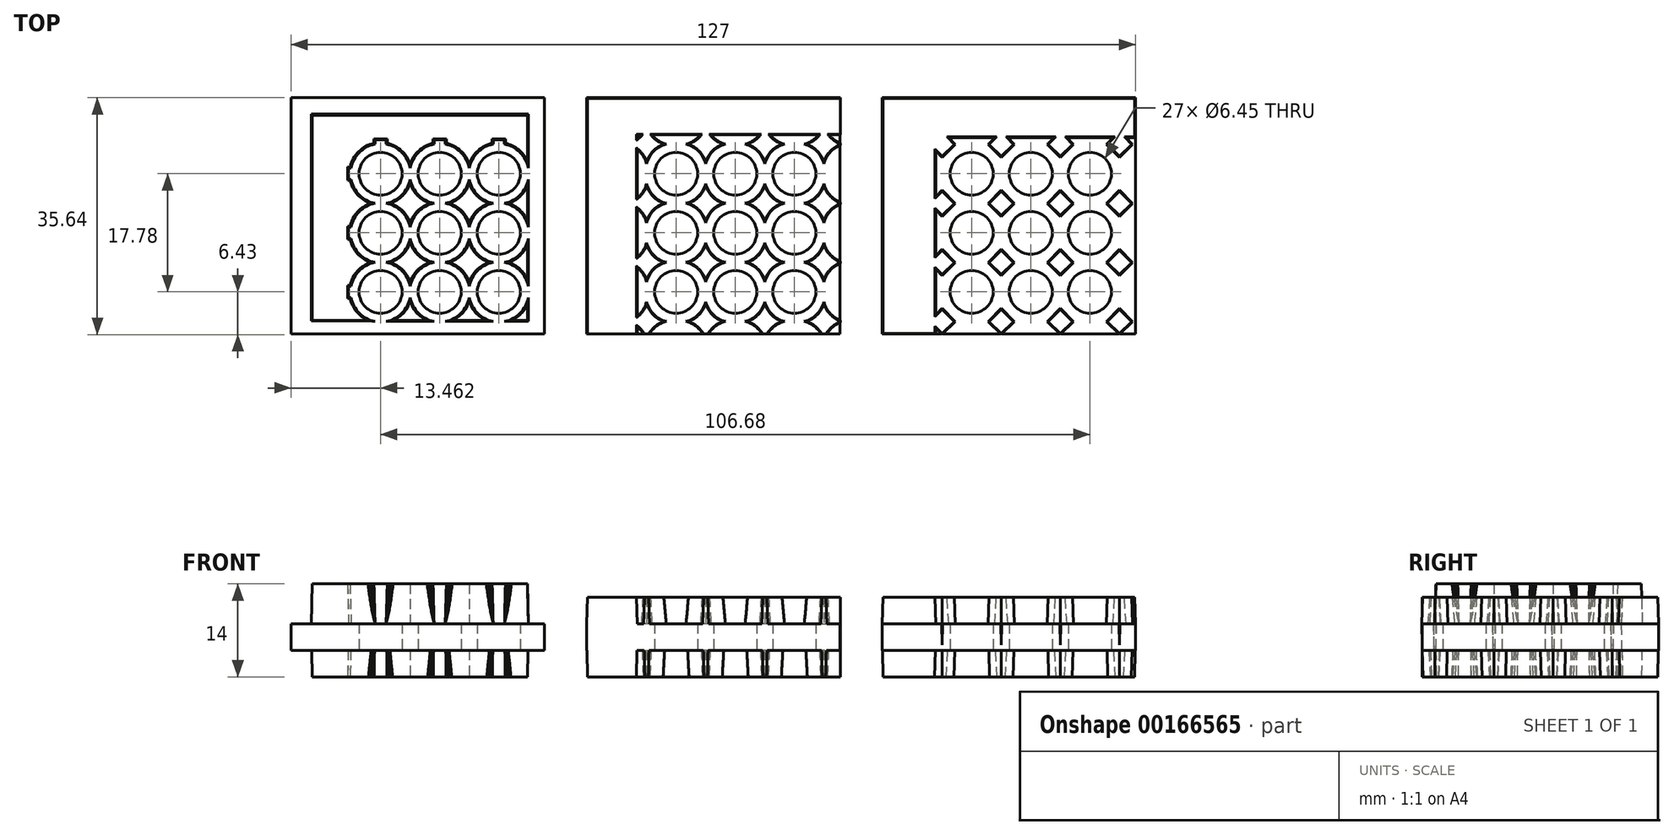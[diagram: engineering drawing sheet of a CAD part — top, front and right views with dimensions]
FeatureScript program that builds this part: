
annotation { "Feature Type Name" : "Feature", "Feature Type Description" : "" }
export const myFeature = defineFeature(function(context is Context, id is Id, definition is map)
    precondition{}
    {
        {
            var Q0;
            Q0=qCreatedBy(makeId("Top.planeOp"),FACE);
            var sketch = newSketch(context, id + "F0", { "sketchPlane" : qUnion([Q0])});
            skLineSegment(sketch, "E0.bottom", {"start": v(0, 0) * mm, "end": v(-38.1, 0) * mm});
            skLineSegment(sketch, "E0.top", {"start": v(0, 35.56) * mm, "end": v(-38.1, 35.56) * mm});
            skLineSegment(sketch, "E0.left", {"start": v(0, 0) * mm, "end": v(0, 35.56) * mm});
            skLineSegment(sketch, "E0.right", {"start": v(-38.1, 0) * mm, "end": v(-38.1, 35.56) * mm});
            skLineSegment(sketch, "E1.bottom", {"start": v(-44.45, 0) * mm, "end": v(-82.55, 0) * mm});
            skLineSegment(sketch, "E1.top", {"start": v(-44.45, 35.56) * mm, "end": v(-82.55, 35.56) * mm});
            skLineSegment(sketch, "E1.left", {"start": v(-44.45, 0) * mm, "end": v(-44.45, 35.56) * mm});
            skLineSegment(sketch, "E1.right", {"start": v(-82.55, 0) * mm, "end": v(-82.55, 35.56) * mm});
            skLineSegment(sketch, "E2.bottom", {"start": v(-88.9, 0) * mm, "end": v(-127, 0) * mm});
            skLineSegment(sketch, "E2.top", {"start": v(-88.9, 35.56) * mm, "end": v(-127, 35.56) * mm});
            skLineSegment(sketch, "E2.left", {"start": v(-88.9, 0) * mm, "end": v(-88.9, 35.56) * mm});
            skLineSegment(sketch, "E2.right", {"start": v(-127, 0) * mm, "end": v(-127, 35.56) * mm});
            skLineSegment(sketch, "E3.bottom", {"start": v(-44.45, 0) * mm, "end": v(-38.1, 0) * mm, "construction": true});
            skLineSegment(sketch, "E3.top", {"start": v(-44.45, 0) * mm, "end": v(-38.1, 0) * mm, "construction": true});
            skLineSegment(sketch, "E3.left", {"start": v(-44.45, 0) * mm, "end": v(-44.45, 0) * mm});
            skLineSegment(sketch, "E3.right", {"start": v(-38.1, 0) * mm, "end": v(-38.1, 0) * mm});
            skLineSegment(sketch, "E4.bottom", {"start": v(-88.9, 0) * mm, "end": v(-82.55, 0) * mm, "construction": true});
            skLineSegment(sketch, "E4.top", {"start": v(-88.9, 0) * mm, "end": v(-82.55, 0) * mm, "construction": true});
            skLineSegment(sketch, "E4.left", {"start": v(-88.9, 0) * mm, "end": v(-88.9, 0) * mm});
            skLineSegment(sketch, "E4.right", {"start": v(-82.55, 0) * mm, "end": v(-82.55, 0) * mm});
            skLineSegment(sketch, "E5.bottom", {"start": v(-88.9, 0) * mm, "end": v(-118.41, 0) * mm, "construction": true});
            skLineSegment(sketch, "E5.top", {"start": v(-88.9, 29.8) * mm, "end": v(-118.41, 29.8) * mm, "construction": true});
            skLineSegment(sketch, "E5.left", {"start": v(-88.9, 0) * mm, "end": v(-88.9, 29.8) * mm, "construction": true});
            skLineSegment(sketch, "E5.right", {"start": v(-118.41, 0) * mm, "end": v(-118.41, 29.8) * mm, "construction": true});
            skLineSegment(sketch, "E6.bottom", {"start": v(-44.45, 0) * mm, "end": v(-73.96, 0) * mm, "construction": true});
            skLineSegment(sketch, "E6.top", {"start": v(-44.45, 29.8) * mm, "end": v(-73.96, 29.8) * mm, "construction": true});
            skLineSegment(sketch, "E6.left", {"start": v(-44.45, 0) * mm, "end": v(-44.45, 29.8) * mm, "construction": true});
            skLineSegment(sketch, "E6.right", {"start": v(-73.96, 0) * mm, "end": v(-73.96, 29.8) * mm, "construction": true});
            skLineSegment(sketch, "E7.bottom", {"start": v(0, 0) * mm, "end": v(-29.51, 0) * mm, "construction": true});
            skLineSegment(sketch, "E7.top", {"start": v(0, 29.8) * mm, "end": v(-29.51, 29.8) * mm, "construction": true});
            skLineSegment(sketch, "E7.left", {"start": v(0, 0) * mm, "end": v(0, 29.8) * mm, "construction": true});
            skLineSegment(sketch, "E7.right", {"start": v(-29.51, 0) * mm, "end": v(-29.51, 29.8) * mm, "construction": true});
            skCircle(sketch, "E8", {"center": v(-113.54, 24.13) * mm, "radius": 3.23 * mm});
            skCircle(sketch, "E9", {"center": v(-69.09, 24.13) * mm, "radius": 3.23 * mm});
            skCircle(sketch, "E10", {"center": v(-24.64, 24.13) * mm, "radius": 3.23 * mm});
            skCircle(sketch, "E11.0.1.0", {"center": v(-113.54, 15.24) * mm, "radius": 3.23 * mm});
            skCircle(sketch, "E11.0.1.1", {"center": v(-69.09, 15.24) * mm, "radius": 3.23 * mm});
            skCircle(sketch, "E11.0.1.2", {"center": v(-24.64, 15.24) * mm, "radius": 3.23 * mm});
            skCircle(sketch, "E11.0.2.0", {"center": v(-113.54, 6.35) * mm, "radius": 3.23 * mm});
            skCircle(sketch, "E11.0.2.1", {"center": v(-69.09, 6.35) * mm, "radius": 3.23 * mm});
            skCircle(sketch, "E11.0.2.2", {"center": v(-24.64, 6.35) * mm, "radius": 3.23 * mm});
            skCircle(sketch, "E11.1.0.0", {"center": v(-104.65, 24.13) * mm, "radius": 3.23 * mm});
            skCircle(sketch, "E11.1.0.1", {"center": v(-60.2, 24.13) * mm, "radius": 3.23 * mm});
            skCircle(sketch, "E11.1.0.2", {"center": v(-15.75, 24.13) * mm, "radius": 3.23 * mm});
            skCircle(sketch, "E11.1.1.0", {"center": v(-104.65, 15.24) * mm, "radius": 3.23 * mm});
            skCircle(sketch, "E11.1.1.1", {"center": v(-60.2, 15.24) * mm, "radius": 3.23 * mm});
            skCircle(sketch, "E11.1.1.2", {"center": v(-15.75, 15.24) * mm, "radius": 3.23 * mm});
            skCircle(sketch, "E11.1.2.0", {"center": v(-104.65, 6.35) * mm, "radius": 3.23 * mm});
            skCircle(sketch, "E11.1.2.1", {"center": v(-60.2, 6.35) * mm, "radius": 3.23 * mm});
            skCircle(sketch, "E11.1.2.2", {"center": v(-15.75, 6.35) * mm, "radius": 3.23 * mm});
            skCircle(sketch, "E11.2.0.0", {"center": v(-95.76, 24.13) * mm, "radius": 3.23 * mm});
            skCircle(sketch, "E11.2.0.1", {"center": v(-51.3, 24.13) * mm, "radius": 3.23 * mm});
            skCircle(sketch, "E11.2.0.2", {"center": v(-6.86, 24.13) * mm, "radius": 3.23 * mm});
            skCircle(sketch, "E11.2.1.0", {"center": v(-95.76, 15.24) * mm, "radius": 3.23 * mm});
            skCircle(sketch, "E11.2.1.1", {"center": v(-51.3, 15.24) * mm, "radius": 3.23 * mm});
            skCircle(sketch, "E11.2.1.2", {"center": v(-6.86, 15.24) * mm, "radius": 3.23 * mm});
            skCircle(sketch, "E11.2.2.0", {"center": v(-95.76, 6.35) * mm, "radius": 3.23 * mm});
            skCircle(sketch, "E11.2.2.1", {"center": v(-51.3, 6.35) * mm, "radius": 3.23 * mm});
            skCircle(sketch, "E11.2.2.2", {"center": v(-6.86, 6.35) * mm, "radius": 3.23 * mm});
            skLineSegment(sketch, "E11.direction1", {"start": v(-113.54, 24.13) * mm, "end": v(-104.65, 24.13) * mm, "construction": true});
            skLineSegment(sketch, "E11.direction2", {"start": v(-113.54, 24.13) * mm, "end": v(-113.54, 15.24) * mm, "construction": true});
            skSolve(sketch);
        }
        {
            var Q0;
            Q0 = qSketchRegion(id + "F0", true);
            extrude(context, id + "F1", {"entities" : qUnion([Q0]), "depth" : 4 * mm});
        }
        {
            var Q0;
            Q0=makeQuery(id+"F1.opExtrude","CAP_FACE",FACE,{"disambiguationData":[OSD([sQuery(id+"F0.wireOp",EDGE,"E2.bottom"),sQuery(id+"F0.wireOp",EDGE,"E2.top"),sQuery(id+"F0.wireOp",EDGE,"E2.left"),sQuery(id+"F0.wireOp",EDGE,"E2.right"),sQuery(id+"F0.wireOp",EDGE,"E8"),sQuery(id+"F0.wireOp",EDGE,"E11.0.1.0"),sQuery(id+"F0.wireOp",EDGE,"E11.0.2.0"),sQuery(id+"F0.wireOp",EDGE,"E11.1.0.0"),sQuery(id+"F0.wireOp",EDGE,"E11.1.1.0"),sQuery(id+"F0.wireOp",EDGE,"E11.1.2.0"),sQuery(id+"F0.wireOp",EDGE,"E11.2.0.0"),sQuery(id+"F0.wireOp",EDGE,"E11.2.1.0"),sQuery(id+"F0.wireOp",EDGE,"E11.2.2.0")])],"isStart":false});
            var sketch = newSketch(context, id + "F2", { "sketchPlane" : qUnion([Q0])});
            skArc(sketch, "E12", {"start": v(-112.7, 19.68) * mm, "mid": v(-110.34, 20.93) * mm, "end": v(-109.1, 23.28) * mm});
            skArc(sketch, "E13", {"start": v(-109.1, 23.28) * mm, "mid": v(-107.85, 20.93) * mm, "end": v(-105.5, 19.68) * mm});
            skArc(sketch, "E14", {"start": v(-109.1, 16.09) * mm, "mid": v(-110.34, 18.44) * mm, "end": v(-112.7, 19.68) * mm});
            skArc(sketch, "E15", {"start": v(-105.5, 19.68) * mm, "mid": v(-107.85, 18.44) * mm, "end": v(-109.1, 16.09) * mm});
            skLineSegment(sketch, "E16", {"start": v(-109.1, 23.28) * mm, "end": v(-109.1, 16.09) * mm, "construction": true});
            skLineSegment(sketch, "E17", {"start": v(-112.7, 19.68) * mm, "end": v(-105.5, 19.68) * mm, "construction": true});
            skPoint(sketch, "E18", {"position": v(-109.1, 19.68) * mm});
            skLineSegment(sketch, "E19", {"start": v(-113.54, 24.13) * mm, "end": v(-104.65, 24.13) * mm, "construction": true});
            skLineSegment(sketch, "E20", {"start": v(-113.54, 15.24) * mm, "end": v(-113.54, 24.13) * mm, "construction": true});
            skPoint(sketch, "E21", {"position": v(-109.1, 24.13) * mm});
            skPoint(sketch, "E22", {"position": v(-113.54, 19.68) * mm});
            skArc(sketch, "E23.0.1.0", {"start": v(-109.1, 14.4) * mm, "mid": v(-107.85, 12.04) * mm, "end": v(-105.5, 10.8) * mm});
            skArc(sketch, "E23.0.1.1", {"start": v(-112.7, 10.8) * mm, "mid": v(-110.34, 12.04) * mm, "end": v(-109.1, 14.4) * mm});
            skArc(sketch, "E23.0.1.2", {"start": v(-109.1, 7.2) * mm, "mid": v(-110.34, 9.55) * mm, "end": v(-112.7, 10.8) * mm});
            skArc(sketch, "E23.0.1.3", {"start": v(-105.5, 10.8) * mm, "mid": v(-107.85, 9.55) * mm, "end": v(-109.1, 7.2) * mm});
            skArc(sketch, "E23.0.2.0", {"start": v(-109.1, 5.5) * mm, "mid": v(-107.85, 3.15) * mm, "end": v(-105.5, 1.9) * mm});
            skArc(sketch, "E23.0.2.1", {"start": v(-112.7, 1.9) * mm, "mid": v(-110.34, 3.15) * mm, "end": v(-109.1, 5.5) * mm});
            skArc(sketch, "E23.1.0.0", {"start": v(-100.2, 23.28) * mm, "mid": v(-98.96, 20.93) * mm, "end": v(-96.6, 19.68) * mm});
            skArc(sketch, "E23.1.0.1", {"start": v(-103.8, 19.68) * mm, "mid": v(-101.45, 20.93) * mm, "end": v(-100.2, 23.28) * mm});
            skArc(sketch, "E23.1.0.2", {"start": v(-100.2, 16.09) * mm, "mid": v(-101.45, 18.44) * mm, "end": v(-103.8, 19.68) * mm});
            skArc(sketch, "E23.1.0.3", {"start": v(-96.6, 19.68) * mm, "mid": v(-98.96, 18.44) * mm, "end": v(-100.2, 16.09) * mm});
            skArc(sketch, "E23.1.1.0", {"start": v(-100.2, 14.4) * mm, "mid": v(-98.96, 12.04) * mm, "end": v(-96.6, 10.8) * mm});
            skArc(sketch, "E23.1.1.1", {"start": v(-103.8, 10.8) * mm, "mid": v(-101.45, 12.04) * mm, "end": v(-100.2, 14.4) * mm});
            skArc(sketch, "E23.1.1.2", {"start": v(-100.2, 7.2) * mm, "mid": v(-101.45, 9.55) * mm, "end": v(-103.8, 10.8) * mm});
            skArc(sketch, "E23.1.1.3", {"start": v(-96.6, 10.8) * mm, "mid": v(-98.96, 9.55) * mm, "end": v(-100.2, 7.2) * mm});
            skArc(sketch, "E23.1.2.0", {"start": v(-100.2, 5.5) * mm, "mid": v(-98.96, 3.15) * mm, "end": v(-96.6, 1.9) * mm});
            skArc(sketch, "E23.1.2.1", {"start": v(-103.8, 1.9) * mm, "mid": v(-101.45, 3.15) * mm, "end": v(-100.2, 5.5) * mm});
            skArc(sketch, "E23.2.0.1", {"start": v(-94.91, 19.68) * mm, "mid": v(-92.56, 20.93) * mm, "end": v(-91.31, 23.28) * mm});
            skArc(sketch, "E23.2.0.2", {"start": v(-91.31, 16.09) * mm, "mid": v(-92.56, 18.44) * mm, "end": v(-94.91, 19.68) * mm});
            skArc(sketch, "E23.2.1.1", {"start": v(-94.91, 10.8) * mm, "mid": v(-92.56, 12.04) * mm, "end": v(-91.31, 14.4) * mm});
            skArc(sketch, "E23.2.1.2", {"start": v(-91.31, 7.2) * mm, "mid": v(-92.56, 9.55) * mm, "end": v(-94.91, 10.8) * mm});
            skArc(sketch, "E23.2.2.1", {"start": v(-94.91, 1.9) * mm, "mid": v(-92.56, 3.15) * mm, "end": v(-91.31, 5.5) * mm});
            skLineSegment(sketch, "E23.direction1", {"start": v(-113.54, 15.24) * mm, "end": v(-104.65, 15.24) * mm, "construction": true});
            skLineSegment(sketch, "E23.direction2", {"start": v(-113.54, 15.24) * mm, "end": v(-113.54, 6.35) * mm, "construction": true});
            skArc(sketch, "E24.0.1.0", {"start": v(-105.5, 28.58) * mm, "mid": v(-107.85, 27.33) * mm, "end": v(-109.1, 24.98) * mm});
            skArc(sketch, "E24.0.1.1", {"start": v(-109.1, 24.98) * mm, "mid": v(-110.34, 27.33) * mm, "end": v(-112.7, 28.58) * mm});
            skArc(sketch, "E24.0.1.2", {"start": v(-100.2, 24.98) * mm, "mid": v(-101.45, 27.33) * mm, "end": v(-103.8, 28.58) * mm});
            skArc(sketch, "E24.0.1.3", {"start": v(-96.6, 28.58) * mm, "mid": v(-98.96, 27.33) * mm, "end": v(-100.2, 24.98) * mm});
            skArc(sketch, "E24.0.1.4", {"start": v(-91.31, 24.98) * mm, "mid": v(-92.56, 27.33) * mm, "end": v(-94.91, 28.58) * mm});
            skLineSegment(sketch, "E24.direction1", {"start": v(-113.54, 15.24) * mm, "end": v(-93.35, 15.24) * mm, "construction": true});
            skArc(sketch, "E25.MirrorCS", {"start": v(-117.98, 24.98) * mm, "mid": v(-116.74, 27.33) * mm, "end": v(-114.38, 28.58) * mm});
            skArc(sketch, "E26.MirrorCS", {"start": v(-114.38, 1.9) * mm, "mid": v(-116.74, 3.15) * mm, "end": v(-117.98, 5.5) * mm});
            skArc(sketch, "E27.MirrorCS", {"start": v(-117.98, 7.2) * mm, "mid": v(-116.74, 9.55) * mm, "end": v(-114.38, 10.8) * mm});
            skArc(sketch, "E28.MirrorCS", {"start": v(-114.38, 10.8) * mm, "mid": v(-116.74, 12.04) * mm, "end": v(-117.98, 14.4) * mm});
            skArc(sketch, "E29.MirrorCS", {"start": v(-117.98, 16.09) * mm, "mid": v(-116.74, 18.44) * mm, "end": v(-114.38, 19.68) * mm});
            skArc(sketch, "E30.MirrorCS", {"start": v(-114.38, 19.68) * mm, "mid": v(-116.74, 20.93) * mm, "end": v(-117.98, 23.28) * mm});
            skLineSegment(sketch, "E31", {"start": v(-114.38, 28.58) * mm, "end": v(-114.38, 29.21) * mm});
            skLineSegment(sketch, "E32", {"start": v(-114.38, 29.21) * mm, "end": v(-112.7, 29.21) * mm});
            skLineSegment(sketch, "E33", {"start": v(-112.7, 29.21) * mm, "end": v(-112.7, 28.58) * mm});
            skLineSegment(sketch, "E34", {"start": v(-105.5, 28.58) * mm, "end": v(-105.5, 29.21) * mm});
            skLineSegment(sketch, "E35", {"start": v(-105.5, 29.21) * mm, "end": v(-103.8, 29.21) * mm});
            skLineSegment(sketch, "E36", {"start": v(-103.8, 29.21) * mm, "end": v(-103.8, 28.58) * mm});
            skLineSegment(sketch, "E37", {"start": v(-96.6, 28.58) * mm, "end": v(-96.6, 29.21) * mm});
            skLineSegment(sketch, "E38", {"start": v(-96.6, 29.21) * mm, "end": v(-94.91, 29.21) * mm});
            skLineSegment(sketch, "E39", {"start": v(-94.91, 29.21) * mm, "end": v(-94.91, 28.58) * mm});
            skLineSegment(sketch, "E40", {"start": v(-117.98, 7.2) * mm, "end": v(-118.33, 7.2) * mm});
            skLineSegment(sketch, "E41", {"start": v(-118.33, 7.2) * mm, "end": v(-118.33, 5.5) * mm});
            skLineSegment(sketch, "E42", {"start": v(-118.33, 5.5) * mm, "end": v(-117.98, 5.5) * mm});
            skLineSegment(sketch, "E43", {"start": v(-91.31, 24.98) * mm, "end": v(-91.31, 33.1) * mm});
            skLineSegment(sketch, "E44", {"start": v(-91.31, 33.1) * mm, "end": v(-123.97, 33.1) * mm});
            skLineSegment(sketch, "E45", {"start": v(-123.97, 33.1) * mm, "end": v(-123.97, 1.98) * mm});
            skLineSegment(sketch, "E46", {"start": v(-123.97, 1.98) * mm, "end": v(-114.38, 1.9) * mm});
            skLineSegment(sketch, "E47", {"start": v(-117.98, 16.09) * mm, "end": v(-118.33, 16.09) * mm});
            skLineSegment(sketch, "E48", {"start": v(-118.33, 16.09) * mm, "end": v(-118.33, 14.4) * mm});
            skLineSegment(sketch, "E49", {"start": v(-118.33, 14.4) * mm, "end": v(-117.98, 14.4) * mm});
            skLineSegment(sketch, "E50", {"start": v(-117.98, 24.98) * mm, "end": v(-118.35, 24.98) * mm});
            skLineSegment(sketch, "E51", {"start": v(-118.35, 24.98) * mm, "end": v(-118.35, 23.28) * mm});
            skLineSegment(sketch, "E52", {"start": v(-118.35, 23.28) * mm, "end": v(-117.98, 23.28) * mm});
            skLineSegment(sketch, "E53", {"start": v(-112.7, 1.9) * mm, "end": v(-105.5, 1.9) * mm});
            skLineSegment(sketch, "E54", {"start": v(-103.8, 1.9) * mm, "end": v(-96.6, 1.9) * mm});
            skLineSegment(sketch, "E55", {"start": v(-91.31, 23.28) * mm, "end": v(-91.31, 16.09) * mm});
            skLineSegment(sketch, "E56", {"start": v(-91.31, 14.4) * mm, "end": v(-91.31, 7.2) * mm});
            skLineSegment(sketch, "E57", {"start": v(-94.91, 1.9) * mm, "end": v(-91.31, 1.93) * mm});
            skLineSegment(sketch, "E58", {"start": v(-91.31, 1.93) * mm, "end": v(-91.31, 5.5) * mm});
            skPoint(sketch, "E59", {"position": v(0, 0) * mm});
            skSolve(sketch);
        }
        {
            var Q0;
            Q0 = qSketchRegion(id + "F2", true);
            extrude(context, id + "F3", {"entities" : qUnion([Q0]), "operationType" : NewBodyOperationType.ADD, "depth" : 6 * mm, "hasDraft" : true, "draftAngle" : 1.5 * degree, "draftPullDirection" : true, "hasSecondDirection" : true, "secondDirectionOppositeDirection" : true, "secondDirectionDepth" : 8 * mm, "hasSecondDirectionDraft" : true, "secondDirectionDraftAngle" : 1 * degree, "secondDirectionDraftPullDirection" : true});
        }
        {
            var Q0;
            Q0=makeQuery(id+"F1.opExtrude","CAP_FACE",FACE,{"disambiguationData":[OSD([sQuery(id+"F0.wireOp",EDGE,"E1.bottom"),sQuery(id+"F0.wireOp",EDGE,"E1.top"),sQuery(id+"F0.wireOp",EDGE,"E1.left"),sQuery(id+"F0.wireOp",EDGE,"E1.right"),sQuery(id+"F0.wireOp",EDGE,"E9"),sQuery(id+"F0.wireOp",EDGE,"E11.0.1.1"),sQuery(id+"F0.wireOp",EDGE,"E11.0.2.1"),sQuery(id+"F0.wireOp",EDGE,"E11.1.0.1"),sQuery(id+"F0.wireOp",EDGE,"E11.1.1.1"),sQuery(id+"F0.wireOp",EDGE,"E11.1.2.1"),sQuery(id+"F0.wireOp",EDGE,"E11.2.0.1"),sQuery(id+"F0.wireOp",EDGE,"E11.2.1.1"),sQuery(id+"F0.wireOp",EDGE,"E11.2.2.1")])],"isStart":false});
            var sketch = newSketch(context, id + "F4", { "sketchPlane" : qUnion([Q0])});
            skArc(sketch, "E60", {"start": v(-67.6, 19.68) * mm, "mid": v(-65.72, 20.76) * mm, "end": v(-64.64, 22.65) * mm});
            skArc(sketch, "E61", {"start": v(-61.68, 19.68) * mm, "mid": v(-63.57, 18.6) * mm, "end": v(-64.64, 16.72) * mm});
            skArc(sketch, "E62", {"start": v(-64.64, 22.65) * mm, "mid": v(-63.57, 20.76) * mm, "end": v(-61.68, 19.68) * mm});
            skLineSegment(sketch, "E63", {"start": v(-82.55, 35.56) * mm, "end": v(-44.45, 35.56) * mm, "construction": true});
            skLineSegment(sketch, "E64", {"start": v(-82.55, 35.56) * mm, "end": v(-82.55, 0) * mm, "construction": true});
            skCircle(sketch, "E65", {"center": v(-69.09, 24.13) * mm, "radius": 3.21 * mm, "construction": true});
            skArc(sketch, "E66", {"start": v(-64.64, 16.72) * mm, "mid": v(-65.72, 18.6) * mm, "end": v(-67.6, 19.68) * mm});
            skCircle(sketch, "E67", {"center": v(-60.2, 24.13) * mm, "radius": 3.21 * mm, "construction": true});
            skCircle(sketch, "E68", {"center": v(-69.09, 15.24) * mm, "radius": 3.21 * mm, "construction": true});
            skLineSegment(sketch, "E69", {"start": v(-69.09, 24.13) * mm, "end": v(-60.2, 24.13) * mm, "construction": true});
            skLineSegment(sketch, "E70", {"start": v(-69.09, 24.13) * mm, "end": v(-69.09, 15.24) * mm, "construction": true});
            skLineSegment(sketch, "E71", {"start": v(-64.64, 22.65) * mm, "end": v(-64.64, 16.72) * mm, "construction": true});
            skLineSegment(sketch, "E72", {"start": v(-67.6, 19.68) * mm, "end": v(-61.68, 19.68) * mm, "construction": true});
            skPoint(sketch, "E73", {"position": v(-64.64, 19.68) * mm});
            skLineSegment(sketch, "E74", {"start": v(-69.09, 15.24) * mm, "end": v(-60.2, 24.13) * mm, "construction": true});
            skLineSegment(sketch, "E75", {"start": v(-69.09, 24.13) * mm, "end": v(-60.2, 15.24) * mm, "construction": true});
            skCircle(sketch, "E76", {"center": v(-60.2, 15.24) * mm, "radius": 3.21 * mm, "construction": true});
            skPoint(sketch, "E77", {"position": v(-64.64, 24.13) * mm});
            skPoint(sketch, "E78", {"position": v(-69.09, 19.68) * mm});
            skArc(sketch, "E79.0.1.0", {"start": v(-64.64, 13.76) * mm, "mid": v(-63.57, 11.87) * mm, "end": v(-61.68, 10.8) * mm});
            skArc(sketch, "E79.0.1.1", {"start": v(-61.68, 10.8) * mm, "mid": v(-63.57, 9.72) * mm, "end": v(-64.64, 7.83) * mm});
            skArc(sketch, "E79.0.1.2", {"start": v(-64.64, 7.83) * mm, "mid": v(-65.72, 9.72) * mm, "end": v(-67.6, 10.8) * mm});
            skArc(sketch, "E79.0.1.3", {"start": v(-67.6, 10.8) * mm, "mid": v(-65.72, 11.87) * mm, "end": v(-64.64, 13.76) * mm});
            skArc(sketch, "E79.0.2.0", {"start": v(-64.64, 4.87) * mm, "mid": v(-63.57, 2.98) * mm, "end": v(-61.68, 1.9) * mm});
            skArc(sketch, "E79.0.2.1", {"start": v(-61.68, 1.9) * mm, "mid": v(-63.57, 0.83) * mm, "end": v(-64.64, -1.06) * mm});
            skArc(sketch, "E79.0.2.2", {"start": v(-64.64, -1.06) * mm, "mid": v(-65.72, 0.83) * mm, "end": v(-67.6, 1.9) * mm});
            skArc(sketch, "E79.0.2.3", {"start": v(-67.6, 1.9) * mm, "mid": v(-65.72, 2.98) * mm, "end": v(-64.64, 4.87) * mm});
            skArc(sketch, "E79.1.0.0", {"start": v(-55.75, 22.65) * mm, "mid": v(-54.68, 20.76) * mm, "end": v(-52.8, 19.68) * mm});
            skArc(sketch, "E79.1.0.1", {"start": v(-52.8, 19.68) * mm, "mid": v(-54.68, 18.6) * mm, "end": v(-55.75, 16.72) * mm});
            skArc(sketch, "E79.1.0.2", {"start": v(-55.75, 16.72) * mm, "mid": v(-56.83, 18.6) * mm, "end": v(-58.72, 19.68) * mm});
            skArc(sketch, "E79.1.0.3", {"start": v(-58.72, 19.68) * mm, "mid": v(-56.83, 20.76) * mm, "end": v(-55.75, 22.65) * mm});
            skArc(sketch, "E79.1.1.0", {"start": v(-55.75, 13.76) * mm, "mid": v(-54.68, 11.87) * mm, "end": v(-52.8, 10.8) * mm});
            skArc(sketch, "E79.1.1.1", {"start": v(-52.8, 10.8) * mm, "mid": v(-54.68, 9.72) * mm, "end": v(-55.75, 7.83) * mm});
            skArc(sketch, "E79.1.1.2", {"start": v(-55.75, 7.83) * mm, "mid": v(-56.83, 9.72) * mm, "end": v(-58.72, 10.8) * mm});
            skArc(sketch, "E79.1.1.3", {"start": v(-58.72, 10.8) * mm, "mid": v(-56.83, 11.87) * mm, "end": v(-55.75, 13.76) * mm});
            skArc(sketch, "E79.1.2.0", {"start": v(-55.75, 4.87) * mm, "mid": v(-54.68, 2.98) * mm, "end": v(-52.8, 1.9) * mm});
            skArc(sketch, "E79.1.2.1", {"start": v(-52.8, 1.9) * mm, "mid": v(-54.68, 0.83) * mm, "end": v(-55.75, -1.06) * mm});
            skArc(sketch, "E79.1.2.2", {"start": v(-55.75, -1.06) * mm, "mid": v(-56.83, 0.83) * mm, "end": v(-58.72, 1.9) * mm});
            skArc(sketch, "E79.1.2.3", {"start": v(-58.72, 1.9) * mm, "mid": v(-56.83, 2.98) * mm, "end": v(-55.75, 4.87) * mm});
            skArc(sketch, "E79.2.0.0", {"start": v(-46.86, 22.65) * mm, "mid": v(-45.79, 20.76) * mm, "end": v(-43.9, 19.68) * mm});
            skArc(sketch, "E79.2.0.1", {"start": v(-43.9, 19.68) * mm, "mid": v(-45.79, 18.6) * mm, "end": v(-46.86, 16.72) * mm});
            skArc(sketch, "E79.2.0.2", {"start": v(-46.86, 16.72) * mm, "mid": v(-47.94, 18.6) * mm, "end": v(-49.83, 19.68) * mm});
            skArc(sketch, "E79.2.0.3", {"start": v(-49.83, 19.68) * mm, "mid": v(-47.94, 20.76) * mm, "end": v(-46.86, 22.65) * mm});
            skArc(sketch, "E79.2.1.0", {"start": v(-46.86, 13.76) * mm, "mid": v(-45.79, 11.87) * mm, "end": v(-43.9, 10.8) * mm});
            skArc(sketch, "E79.2.1.1", {"start": v(-43.9, 10.8) * mm, "mid": v(-45.79, 9.72) * mm, "end": v(-46.86, 7.83) * mm});
            skArc(sketch, "E79.2.1.2", {"start": v(-46.86, 7.83) * mm, "mid": v(-47.94, 9.72) * mm, "end": v(-49.83, 10.8) * mm});
            skArc(sketch, "E79.2.1.3", {"start": v(-49.83, 10.8) * mm, "mid": v(-47.94, 11.87) * mm, "end": v(-46.86, 13.76) * mm});
            skArc(sketch, "E79.2.2.0", {"start": v(-46.86, 4.87) * mm, "mid": v(-45.79, 2.98) * mm, "end": v(-43.9, 1.9) * mm});
            skArc(sketch, "E79.2.2.1", {"start": v(-43.9, 1.9) * mm, "mid": v(-45.79, 0.83) * mm, "end": v(-46.86, -1.06) * mm});
            skArc(sketch, "E79.2.2.2", {"start": v(-46.86, -1.06) * mm, "mid": v(-47.94, 0.83) * mm, "end": v(-49.83, 1.9) * mm});
            skArc(sketch, "E79.2.2.3", {"start": v(-49.83, 1.9) * mm, "mid": v(-47.94, 2.98) * mm, "end": v(-46.86, 4.87) * mm});
            skLineSegment(sketch, "E79.direction1", {"start": v(-68.64, 15.69) * mm, "end": v(-59.75, 15.69) * mm, "construction": true});
            skLineSegment(sketch, "E79.direction2", {"start": v(-68.64, 15.69) * mm, "end": v(-68.64, 6.8) * mm, "construction": true});
            skArc(sketch, "E80.0.3.0", {"start": v(-46.86, 31.54) * mm, "mid": v(-45.79, 29.65) * mm, "end": v(-43.9, 28.57) * mm});
            skArc(sketch, "E80.0.3.1", {"start": v(-49.83, 28.57) * mm, "mid": v(-47.94, 29.65) * mm, "end": v(-46.86, 31.54) * mm});
            skArc(sketch, "E80.0.3.2", {"start": v(-46.86, 25.61) * mm, "mid": v(-47.94, 27.5) * mm, "end": v(-49.83, 28.57) * mm});
            skArc(sketch, "E80.0.3.3", {"start": v(-43.9, 28.57) * mm, "mid": v(-45.79, 27.5) * mm, "end": v(-46.86, 25.61) * mm});
            skArc(sketch, "E80.1.3.0", {"start": v(-55.75, 31.54) * mm, "mid": v(-54.68, 29.65) * mm, "end": v(-52.8, 28.57) * mm});
            skArc(sketch, "E80.1.3.1", {"start": v(-58.72, 28.57) * mm, "mid": v(-56.83, 29.65) * mm, "end": v(-55.75, 31.54) * mm});
            skArc(sketch, "E80.1.3.2", {"start": v(-55.75, 25.61) * mm, "mid": v(-56.83, 27.5) * mm, "end": v(-58.72, 28.57) * mm});
            skArc(sketch, "E80.1.3.3", {"start": v(-52.8, 28.57) * mm, "mid": v(-54.68, 27.5) * mm, "end": v(-55.75, 25.61) * mm});
            skArc(sketch, "E80.2.3.0", {"start": v(-64.64, 31.54) * mm, "mid": v(-63.57, 29.65) * mm, "end": v(-61.68, 28.57) * mm});
            skArc(sketch, "E80.2.3.1", {"start": v(-67.6, 28.57) * mm, "mid": v(-65.72, 29.65) * mm, "end": v(-64.64, 31.54) * mm});
            skArc(sketch, "E80.2.3.2", {"start": v(-64.64, 25.61) * mm, "mid": v(-65.72, 27.5) * mm, "end": v(-67.6, 28.57) * mm});
            skArc(sketch, "E80.2.3.3", {"start": v(-61.68, 28.57) * mm, "mid": v(-63.57, 27.5) * mm, "end": v(-64.64, 25.61) * mm});
            skArc(sketch, "E80.3.0.0", {"start": v(-73.53, 4.87) * mm, "mid": v(-72.46, 2.98) * mm, "end": v(-70.57, 1.9) * mm});
            skArc(sketch, "E80.3.0.1", {"start": v(-76.5, 1.9) * mm, "mid": v(-74.61, 2.98) * mm, "end": v(-73.53, 4.87) * mm});
            skArc(sketch, "E80.3.0.2", {"start": v(-73.53, -1.06) * mm, "mid": v(-74.61, 0.83) * mm, "end": v(-76.5, 1.9) * mm});
            skArc(sketch, "E80.3.0.3", {"start": v(-70.57, 1.9) * mm, "mid": v(-72.46, 0.83) * mm, "end": v(-73.53, -1.06) * mm});
            skArc(sketch, "E80.3.1.0", {"start": v(-73.53, 13.76) * mm, "mid": v(-72.46, 11.87) * mm, "end": v(-70.57, 10.8) * mm});
            skArc(sketch, "E80.3.1.1", {"start": v(-76.5, 10.8) * mm, "mid": v(-74.61, 11.87) * mm, "end": v(-73.53, 13.76) * mm});
            skArc(sketch, "E80.3.1.2", {"start": v(-73.53, 7.83) * mm, "mid": v(-74.61, 9.72) * mm, "end": v(-76.5, 10.8) * mm});
            skArc(sketch, "E80.3.1.3", {"start": v(-70.57, 10.8) * mm, "mid": v(-72.46, 9.72) * mm, "end": v(-73.53, 7.83) * mm});
            skArc(sketch, "E80.3.2.0", {"start": v(-73.53, 22.65) * mm, "mid": v(-72.46, 20.76) * mm, "end": v(-70.57, 19.68) * mm});
            skArc(sketch, "E80.3.2.1", {"start": v(-76.5, 19.68) * mm, "mid": v(-74.61, 20.76) * mm, "end": v(-73.53, 22.65) * mm});
            skArc(sketch, "E80.3.2.2", {"start": v(-73.53, 16.72) * mm, "mid": v(-74.61, 18.6) * mm, "end": v(-76.5, 19.68) * mm});
            skArc(sketch, "E80.3.2.3", {"start": v(-70.57, 19.68) * mm, "mid": v(-72.46, 18.6) * mm, "end": v(-73.53, 16.72) * mm});
            skArc(sketch, "E80.3.3.0", {"start": v(-73.53, 31.54) * mm, "mid": v(-72.46, 29.65) * mm, "end": v(-70.57, 28.57) * mm});
            skArc(sketch, "E80.3.3.1", {"start": v(-76.5, 28.57) * mm, "mid": v(-74.61, 29.65) * mm, "end": v(-73.53, 31.54) * mm});
            skArc(sketch, "E80.3.3.2", {"start": v(-73.53, 25.61) * mm, "mid": v(-74.61, 27.5) * mm, "end": v(-76.5, 28.57) * mm});
            skArc(sketch, "E80.3.3.3", {"start": v(-70.57, 28.57) * mm, "mid": v(-72.46, 27.5) * mm, "end": v(-73.53, 25.61) * mm});
            skLineSegment(sketch, "E80.direction1", {"start": v(-50.86, -2.1) * mm, "end": v(-59.75, -2.1) * mm, "construction": true});
            skLineSegment(sketch, "E80.direction2", {"start": v(-50.86, -2.1) * mm, "end": v(-50.86, 6.8) * mm, "construction": true});
            skLineSegment(sketch, "E81.top", {"start": v(-43.9, 35.56) * mm, "end": v(-82.55, 35.56) * mm});
            skLineSegment(sketch, "E81.right", {"start": v(-82.55, 28.57) * mm, "end": v(-82.55, 35.56) * mm});
            skLineSegment(sketch, "E82.top", {"start": v(-73.53, 35.56) * mm, "end": v(-82.55, 35.56) * mm});
            skLineSegment(sketch, "E82.right", {"start": v(-82.55, -1.06) * mm, "end": v(-82.55, 35.56) * mm});
            skLineSegment(sketch, "E83", {"start": v(-82.55, -1.06) * mm, "end": v(-74.93, -1.06) * mm});
            skLineSegment(sketch, "E84", {"start": v(-74.93, -1.06) * mm, "end": v(-74.93, 29.97) * mm});
            skLineSegment(sketch, "E85", {"start": v(-74.93, 29.97) * mm, "end": v(-44, 29.97) * mm});
            skLineSegment(sketch, "E86", {"start": v(-44, 29.97) * mm, "end": v(-43.9, 35.56) * mm});
            skSolve(sketch);
        }
        {
            var Q0;
            Q0 = qSketchRegion(id + "F4", true);
            extrude(context, id + "F5", {"entities" : qUnion([Q0]), "operationType" : NewBodyOperationType.ADD, "depth" : 4 * mm, "hasDraft" : true, "draftAngle" : 1.5 * degree, "draftPullDirection" : true, "hasSecondDirection" : true, "secondDirectionOppositeDirection" : true, "secondDirectionDepth" : 8 * mm, "hasSecondDirectionDraft" : true, "secondDirectionDraftAngle" : 1 * degree, "secondDirectionDraftPullDirection" : true});
        }
        {
            var Q0;
            Q0=makeQuery(id+"F5.opExtrude","CAP_FACE",FACE,{"disambiguationData":[OSD([sQuery(id+"F4.wireOp",EDGE,"E80.0.3.2"),sQuery(id+"F4.wireOp",EDGE,"E80.0.3.3"),sQuery(id+"F4.wireOp",EDGE,"E80.1.3.2"),sQuery(id+"F4.wireOp",EDGE,"E80.1.3.3"),sQuery(id+"F4.wireOp",EDGE,"E80.2.3.2"),sQuery(id+"F4.wireOp",EDGE,"E80.2.3.3"),sQuery(id+"F4.wireOp",EDGE,"E80.3.0.0"),sQuery(id+"F4.wireOp",EDGE,"E80.3.0.3"),sQuery(id+"F4.wireOp",EDGE,"E80.3.1.0"),sQuery(id+"F4.wireOp",EDGE,"E80.3.1.3"),sQuery(id+"F4.wireOp",EDGE,"E80.3.2.0"),sQuery(id+"F4.wireOp",EDGE,"E80.3.2.3"),sQuery(id+"F4.wireOp",EDGE,"E80.3.3.1"),sQuery(id+"F4.wireOp",EDGE,"E80.3.3.3"),sQuery(id+"F4.wireOp",EDGE,"E81.bottom"),sQuery(id+"F4.wireOp",EDGE,"E81.top"),sQuery(id+"F4.wireOp",EDGE,"E81.left"),sQuery(id+"F4.wireOp",EDGE,"E82.bottom"),sQuery(id+"F4.wireOp",EDGE,"E82.top"),sQuery(id+"F4.wireOp",EDGE,"E82.left"),sQuery(id+"F4.wireOp",EDGE,"E82.right")])],"isStart":false});
            var sketch = newSketch(context, id + "F6", { "sketchPlane" : qUnion([Q0])});
            skLineSegment(sketch, "E87.bottom", {"start": v(-44.38, 0) * mm, "end": v(-82.92, 0) * mm});
            skLineSegment(sketch, "E87.top", {"start": v(-44.38, -11.5) * mm, "end": v(-82.92, -11.5) * mm});
            skLineSegment(sketch, "E87.left", {"start": v(-44.38, 0) * mm, "end": v(-44.38, -11.5) * mm});
            skLineSegment(sketch, "E87.right", {"start": v(-82.92, 0) * mm, "end": v(-82.92, -11.5) * mm});
            skLineSegment(sketch, "E88.bottom", {"start": v(-44.38, 0) * mm, "end": v(-40.56, 0) * mm});
            skLineSegment(sketch, "E88.top", {"start": v(-44.38, 38.5) * mm, "end": v(-40.56, 38.5) * mm});
            skLineSegment(sketch, "E88.left", {"start": v(-44.38, 0) * mm, "end": v(-44.38, 38.5) * mm});
            skLineSegment(sketch, "E88.right", {"start": v(-40.56, 0) * mm, "end": v(-40.56, 38.5) * mm});
            skSolve(sketch);
        }
        {
            var Q0;
            Q0 = qSketchRegion(id + "F6", true);
            extrude(context, id + "F7", {"entities" : qUnion([Q0]), "operationType" : NewBodyOperationType.REMOVE, "oppositeDirection" : true, "depth" : 25.4 * mm});
        }
        {
            var Q0;
            Q0=makeQuery(id+"F1.opExtrude","CAP_FACE",FACE,{"disambiguationData":[OSD([sQuery(id+"F0.wireOp",EDGE,"E0.bottom"),sQuery(id+"F0.wireOp",EDGE,"E0.top"),sQuery(id+"F0.wireOp",EDGE,"E0.left"),sQuery(id+"F0.wireOp",EDGE,"E0.right"),sQuery(id+"F0.wireOp",EDGE,"E10"),sQuery(id+"F0.wireOp",EDGE,"E11.0.1.2"),sQuery(id+"F0.wireOp",EDGE,"E11.0.2.2"),sQuery(id+"F0.wireOp",EDGE,"E11.1.0.2"),sQuery(id+"F0.wireOp",EDGE,"E11.1.1.2"),sQuery(id+"F0.wireOp",EDGE,"E11.1.2.2"),sQuery(id+"F0.wireOp",EDGE,"E11.2.0.2"),sQuery(id+"F0.wireOp",EDGE,"E11.2.1.2"),sQuery(id+"F0.wireOp",EDGE,"E11.2.2.2")])],"isStart":false});
            var sketch = newSketch(context, id + "F8", { "sketchPlane" : qUnion([Q0])});
            skLineSegment(sketch, "E89", {"start": v(0, 33.02) * mm, "end": v(-33.53, 33.02) * mm, "construction": true});
            skLineSegment(sketch, "E90", {"start": v(-33.53, 33.02) * mm, "end": v(-33.53, 0) * mm, "construction": true});
            skLineSegment(sketch, "E91", {"start": v(-29.07, 26.6) * mm, "end": v(-27.1, 28.57) * mm});
            skPoint(sketch, "E91.startSnap0", {"position": v(-29.07, 28.57) * mm});
            skLineSegment(sketch, "E92", {"start": v(-27.1, 28.57) * mm, "end": v(-29.07, 30.54) * mm});
            skLineSegment(sketch, "E93", {"start": v(-29.07, 30.54) * mm, "end": v(-31.05, 28.57) * mm});
            skLineSegment(sketch, "E94", {"start": v(-31.05, 28.57) * mm, "end": v(-29.07, 26.6) * mm});
            skPoint(sketch, "E95", {"position": v(-28.09, 27.58) * mm});
            skLineSegment(sketch, "E96", {"start": v(-33.53, 33.02) * mm, "end": v(-24.64, 24.13) * mm, "construction": true});
            skLineSegment(sketch, "E97", {"start": v(-24.64, 24.13) * mm, "end": v(-15.75, 15.24) * mm, "construction": true});
            skPoint(sketch, "E98", {"position": v(-20.2, 19.68) * mm});
            skLineSegment(sketch, "E99.0.1.0", {"start": v(-29.07, 17.7) * mm, "end": v(-27.1, 19.68) * mm});
            skLineSegment(sketch, "E99.0.1.1", {"start": v(-27.1, 19.68) * mm, "end": v(-29.07, 21.65) * mm});
            skLineSegment(sketch, "E99.0.1.2", {"start": v(-29.07, 21.65) * mm, "end": v(-31.05, 19.68) * mm});
            skLineSegment(sketch, "E99.0.1.3", {"start": v(-31.05, 19.68) * mm, "end": v(-29.07, 17.7) * mm});
            skLineSegment(sketch, "E99.0.2.0", {"start": v(-29.07, 8.81) * mm, "end": v(-27.1, 10.79) * mm});
            skLineSegment(sketch, "E99.0.2.1", {"start": v(-27.1, 10.79) * mm, "end": v(-29.07, 12.76) * mm});
            skLineSegment(sketch, "E99.0.2.2", {"start": v(-29.07, 12.76) * mm, "end": v(-31.05, 10.79) * mm});
            skLineSegment(sketch, "E99.0.2.3", {"start": v(-31.05, 10.79) * mm, "end": v(-29.07, 8.81) * mm});
            skLineSegment(sketch, "E99.0.3.0", {"start": v(-29.07, -0.08) * mm, "end": v(-27.1, 1.9) * mm});
            skLineSegment(sketch, "E99.0.3.1", {"start": v(-27.1, 1.9) * mm, "end": v(-29.07, 3.87) * mm});
            skLineSegment(sketch, "E99.0.3.2", {"start": v(-29.07, 3.87) * mm, "end": v(-31.05, 1.9) * mm});
            skLineSegment(sketch, "E99.0.3.3", {"start": v(-31.05, 1.9) * mm, "end": v(-29.07, -0.08) * mm});
            skLineSegment(sketch, "E99.1.0.0", {"start": v(-20.18, 26.6) * mm, "end": v(-18.2, 28.57) * mm});
            skLineSegment(sketch, "E99.1.0.1", {"start": v(-18.2, 28.57) * mm, "end": v(-20.18, 30.54) * mm});
            skLineSegment(sketch, "E99.1.0.2", {"start": v(-20.18, 30.54) * mm, "end": v(-22.16, 28.57) * mm});
            skLineSegment(sketch, "E99.1.0.3", {"start": v(-22.16, 28.57) * mm, "end": v(-20.18, 26.6) * mm});
            skLineSegment(sketch, "E99.1.1.0", {"start": v(-20.18, 17.7) * mm, "end": v(-18.2, 19.68) * mm});
            skLineSegment(sketch, "E99.1.1.1", {"start": v(-18.2, 19.68) * mm, "end": v(-20.18, 21.65) * mm});
            skLineSegment(sketch, "E99.1.1.2", {"start": v(-20.18, 21.65) * mm, "end": v(-22.16, 19.68) * mm});
            skLineSegment(sketch, "E99.1.1.3", {"start": v(-22.16, 19.68) * mm, "end": v(-20.18, 17.7) * mm});
            skLineSegment(sketch, "E99.1.2.0", {"start": v(-20.18, 8.81) * mm, "end": v(-18.2, 10.79) * mm});
            skLineSegment(sketch, "E99.1.2.1", {"start": v(-18.2, 10.79) * mm, "end": v(-20.18, 12.76) * mm});
            skLineSegment(sketch, "E99.1.2.2", {"start": v(-20.18, 12.76) * mm, "end": v(-22.16, 10.79) * mm});
            skLineSegment(sketch, "E99.1.2.3", {"start": v(-22.16, 10.79) * mm, "end": v(-20.18, 8.81) * mm});
            skLineSegment(sketch, "E99.1.3.0", {"start": v(-20.18, -0.08) * mm, "end": v(-18.2, 1.9) * mm});
            skLineSegment(sketch, "E99.1.3.1", {"start": v(-18.2, 1.9) * mm, "end": v(-20.18, 3.87) * mm});
            skLineSegment(sketch, "E99.1.3.2", {"start": v(-20.18, 3.87) * mm, "end": v(-22.16, 1.9) * mm});
            skLineSegment(sketch, "E99.1.3.3", {"start": v(-22.16, 1.9) * mm, "end": v(-20.18, -0.08) * mm});
            skLineSegment(sketch, "E99.2.0.0", {"start": v(-11.3, 26.6) * mm, "end": v(-9.32, 28.57) * mm});
            skLineSegment(sketch, "E99.2.0.1", {"start": v(-9.32, 28.57) * mm, "end": v(-11.3, 30.54) * mm});
            skLineSegment(sketch, "E99.2.0.2", {"start": v(-11.3, 30.54) * mm, "end": v(-13.27, 28.57) * mm});
            skLineSegment(sketch, "E99.2.0.3", {"start": v(-13.27, 28.57) * mm, "end": v(-11.3, 26.6) * mm});
            skLineSegment(sketch, "E99.2.1.0", {"start": v(-11.3, 17.7) * mm, "end": v(-9.32, 19.68) * mm});
            skLineSegment(sketch, "E99.2.1.1", {"start": v(-9.32, 19.68) * mm, "end": v(-11.3, 21.65) * mm});
            skLineSegment(sketch, "E99.2.1.2", {"start": v(-11.3, 21.65) * mm, "end": v(-13.27, 19.68) * mm});
            skLineSegment(sketch, "E99.2.1.3", {"start": v(-13.27, 19.68) * mm, "end": v(-11.3, 17.7) * mm});
            skLineSegment(sketch, "E99.2.2.0", {"start": v(-11.3, 8.81) * mm, "end": v(-9.32, 10.79) * mm});
            skLineSegment(sketch, "E99.2.2.1", {"start": v(-9.32, 10.79) * mm, "end": v(-11.3, 12.76) * mm});
            skLineSegment(sketch, "E99.2.2.2", {"start": v(-11.3, 12.76) * mm, "end": v(-13.27, 10.79) * mm});
            skLineSegment(sketch, "E99.2.2.3", {"start": v(-13.27, 10.79) * mm, "end": v(-11.3, 8.81) * mm});
            skLineSegment(sketch, "E99.2.3.0", {"start": v(-11.3, -0.08) * mm, "end": v(-9.32, 1.9) * mm});
            skLineSegment(sketch, "E99.2.3.1", {"start": v(-9.32, 1.9) * mm, "end": v(-11.3, 3.87) * mm});
            skLineSegment(sketch, "E99.2.3.2", {"start": v(-11.3, 3.87) * mm, "end": v(-13.27, 1.9) * mm});
            skLineSegment(sketch, "E99.2.3.3", {"start": v(-13.27, 1.9) * mm, "end": v(-11.3, -0.08) * mm});
            skLineSegment(sketch, "E99.3.0.0", {"start": v(-2.4, 26.6) * mm, "end": v(-0.43, 28.57) * mm});
            skLineSegment(sketch, "E99.3.0.1", {"start": v(-0.43, 28.57) * mm, "end": v(-2.4, 30.54) * mm});
            skLineSegment(sketch, "E99.3.0.2", {"start": v(-2.4, 30.54) * mm, "end": v(-4.38, 28.57) * mm});
            skLineSegment(sketch, "E99.3.0.3", {"start": v(-4.38, 28.57) * mm, "end": v(-2.4, 26.6) * mm});
            skLineSegment(sketch, "E99.3.1.0", {"start": v(-2.4, 17.7) * mm, "end": v(-0.43, 19.68) * mm});
            skLineSegment(sketch, "E99.3.1.1", {"start": v(-0.43, 19.68) * mm, "end": v(-2.4, 21.65) * mm});
            skLineSegment(sketch, "E99.3.1.2", {"start": v(-2.4, 21.65) * mm, "end": v(-4.38, 19.68) * mm});
            skLineSegment(sketch, "E99.3.1.3", {"start": v(-4.38, 19.68) * mm, "end": v(-2.4, 17.7) * mm});
            skLineSegment(sketch, "E99.3.2.0", {"start": v(-2.4, 8.81) * mm, "end": v(-0.43, 10.79) * mm});
            skLineSegment(sketch, "E99.3.2.1", {"start": v(-0.43, 10.79) * mm, "end": v(-2.4, 12.76) * mm});
            skLineSegment(sketch, "E99.3.2.2", {"start": v(-2.4, 12.76) * mm, "end": v(-4.38, 10.79) * mm});
            skLineSegment(sketch, "E99.3.2.3", {"start": v(-4.38, 10.79) * mm, "end": v(-2.4, 8.81) * mm});
            skLineSegment(sketch, "E99.3.3.0", {"start": v(-2.4, -0.08) * mm, "end": v(-0.43, 1.9) * mm});
            skLineSegment(sketch, "E99.3.3.1", {"start": v(-0.43, 1.9) * mm, "end": v(-2.4, 3.87) * mm});
            skLineSegment(sketch, "E99.3.3.2", {"start": v(-2.4, 3.87) * mm, "end": v(-4.38, 1.9) * mm});
            skLineSegment(sketch, "E99.3.3.3", {"start": v(-4.38, 1.9) * mm, "end": v(-2.4, -0.08) * mm});
            skLineSegment(sketch, "E99.direction1", {"start": v(-29.07, 26.6) * mm, "end": v(-20.18, 26.6) * mm, "construction": true});
            skLineSegment(sketch, "E99.direction2", {"start": v(-29.07, 26.6) * mm, "end": v(-29.07, 17.7) * mm, "construction": true});
            skPoint(sketch, "E100.oppositeSnap0", {"position": v(-30.06, 29.55) * mm});
            skLineSegment(sketch, "E100.bottom", {"start": v(0, 35.56) * mm, "end": v(-38.1, 35.56) * mm});
            skLineSegment(sketch, "E100.top", {"start": v(0, 29.55) * mm, "end": v(-38.1, 29.55) * mm});
            skLineSegment(sketch, "E100.left", {"start": v(0, 35.56) * mm, "end": v(0, 29.55) * mm});
            skLineSegment(sketch, "E100.right", {"start": v(-38.1, 35.56) * mm, "end": v(-38.1, 29.55) * mm});
            skPoint(sketch, "E101.oppositeSnap0", {"position": v(-30.06, 11.77) * mm});
            skLineSegment(sketch, "E101.bottom", {"start": v(-38.1, 35.56) * mm, "end": v(-30.06, 35.56) * mm});
            skLineSegment(sketch, "E101.top", {"start": v(-38.1, 0) * mm, "end": v(-30.06, 0) * mm});
            skLineSegment(sketch, "E101.left", {"start": v(-38.1, 35.56) * mm, "end": v(-38.1, 0) * mm});
            skLineSegment(sketch, "E101.right", {"start": v(-30.06, 35.56) * mm, "end": v(-30.06, 0) * mm});
            skSolve(sketch);
        }
        {
            var Q0;
            Q0 = qSketchRegion(id + "F8", true);
            extrude(context, id + "F9", {"entities" : qUnion([Q0]), "operationType" : NewBodyOperationType.ADD, "depth" : 4 * mm, "hasDraft" : true, "draftAngle" : 1.5 * degree, "draftPullDirection" : true, "hasSecondDirection" : true, "secondDirectionOppositeDirection" : true, "secondDirectionDepth" : 8 * mm, "hasSecondDirectionDraft" : true, "secondDirectionDraftAngle" : 1 * degree, "secondDirectionDraftPullDirection" : true});
        }
    });
